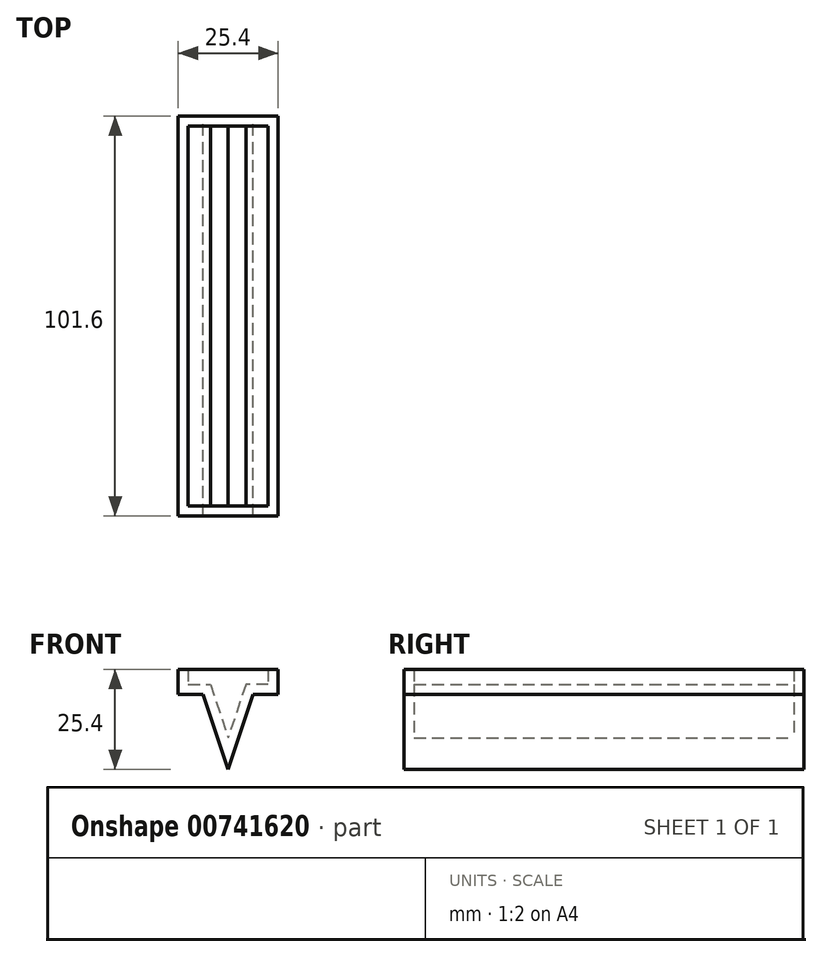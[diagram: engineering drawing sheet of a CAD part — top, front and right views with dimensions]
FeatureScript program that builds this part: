
annotation { "Feature Type Name" : "Feature", "Feature Type Description" : "" }
export const myFeature = defineFeature(function(context is Context, id is Id, definition is map)
    precondition{}
    {
        {
            var Q0;
            Q0=qCreatedBy(makeId("Front.planeOp"),FACE);
            var sketch = newSketch(context, id + "F0", { "sketchPlane" : qUnion([Q0])});
            skLineSegment(sketch, "E0", {"start": v(-25.4, 0) * mm, "end": v(0, 0) * mm});
            skLineSegment(sketch, "E1", {"start": v(0, 0) * mm, "end": v(0, -6.35) * mm});
            skLineSegment(sketch, "E2", {"start": v(0, -6.35) * mm, "end": v(-6.35, -6.35) * mm});
            skLineSegment(sketch, "E3", {"start": v(-6.35, -6.35) * mm, "end": v(-12.7, -25.4) * mm});
            skLineSegment(sketch, "E4", {"start": v(-25.4, 0) * mm, "end": v(-25.4, -6.35) * mm});
            skLineSegment(sketch, "E5", {"start": v(-25.4, -6.35) * mm, "end": v(-19.05, -6.35) * mm});
            skLineSegment(sketch, "E6", {"start": v(-19.05, -6.35) * mm, "end": v(-12.7, -25.4) * mm});
            skSolve(sketch);
        }
        {
            var Q0;
            Q0=makeQuery(id+"F0.imprint","IMPRINT",FACE,{"disambiguationData":[TD([[makeQuery(id+"F0.imprint","IMPRINT",EDGE,{"derivedFrom":sQuery(id+"F0.wireOp",EDGE,"E0")}),-1.0]])]});
            extrude(context, id + "F1", {"entities" : qUnion([Q0]), "depth" : 101.6 * mm, "offsetDistance" : 25.4 * mm});
        }
        {
            var Q0;
            Q0=makeQuery(id+"F1.opExtrude","SWEPT_FACE",FACE,{"disambiguationData":[OSD([sQuery(id+"F0.wireOp",EDGE,"E0")])]});
            shell(context, id + "F2", {"entities" : qUnion([Q0]), "thickness" : 2.54 * mm});
        }
    });
